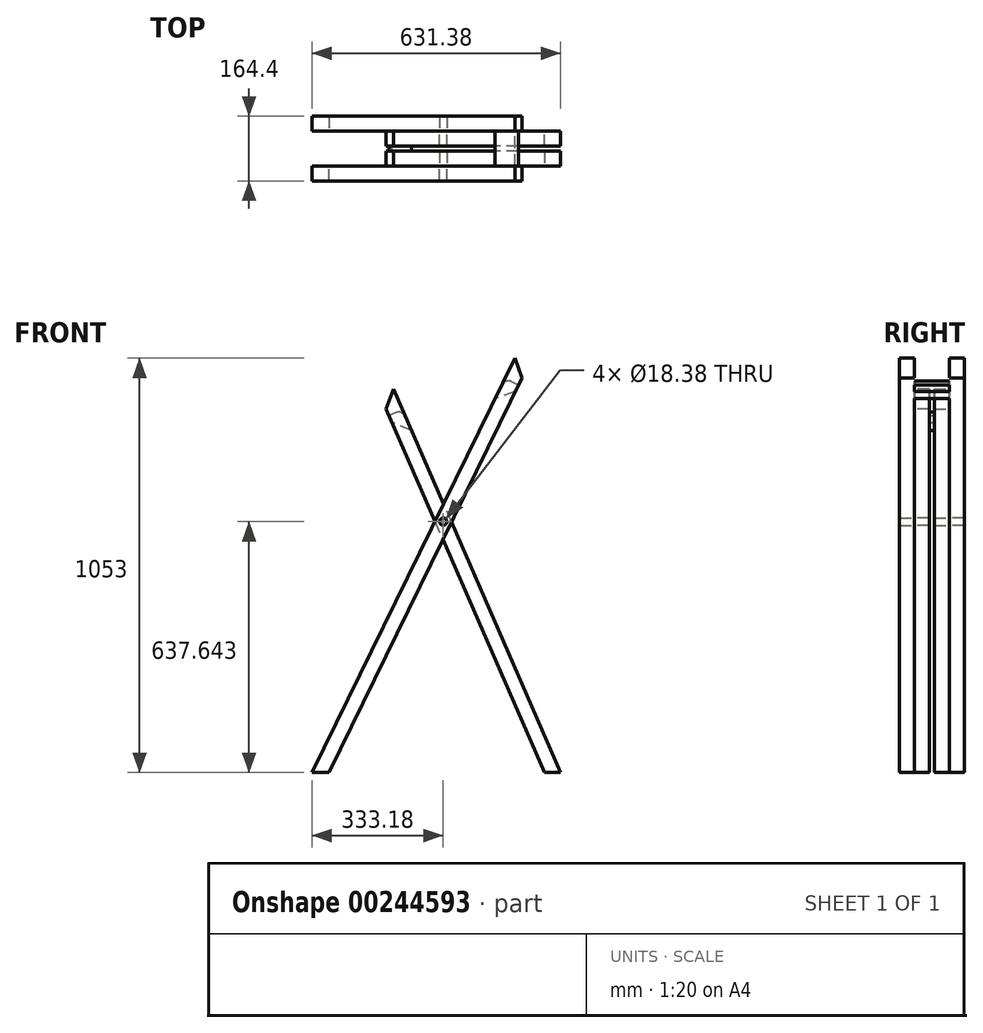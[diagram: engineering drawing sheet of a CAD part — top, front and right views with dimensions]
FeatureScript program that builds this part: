
annotation { "Feature Type Name" : "Feature", "Feature Type Description" : "" }
export const myFeature = defineFeature(function(context is Context, id is Id, definition is map)
    precondition{}
    {
        {
            assignVariable(context, id + "F0", {"name" : "seatWidth", "anyValue" : 12});
        }
        {
            var Q0;
            Q0=qCreatedBy(makeId("Front.planeOp"),FACE);
            var sketch = newSketch(context, id + "F1", { "sketchPlane" : qUnion([Q0])});
            skLineSegment(sketch, "E0", {"start": v(-458.88, 959.2) * mm, "end": v(-443.68, 924.27) * mm, "construction": true});
            skLineSegment(sketch, "E1", {"start": v(-41.55, 0) * mm, "end": v(0, 0) * mm});
            skLineSegment(sketch, "E2", {"start": v(0, 0) * mm, "end": v(-423.94, 974.4) * mm});
            skLineSegment(sketch, "E3", {"start": v(-423.94, 974.4) * mm, "end": v(-458.88, 959.2) * mm, "construction": true});
            skLineSegment(sketch, "E4", {"start": v(-631.38, 0) * mm, "end": v(-588.97, 0) * mm});
            skLineSegment(sketch, "E5", {"start": v(-588.97, 0) * mm, "end": v(-98.71, 1002.03) * mm});
            skLineSegment(sketch, "E6", {"start": v(-81.97, 1036.25) * mm, "end": v(-116.2, 1053) * mm, "construction": true});
            skLineSegment(sketch, "E7", {"start": v(-116.2, 1053) * mm, "end": v(-631.38, 0) * mm});
            skLineSegment(sketch, "E8", {"start": v(-441.41, 966.8) * mm, "end": v(-20.77, 0) * mm, "construction": true});
            skLineSegment(sketch, "E9", {"start": v(-610.17, 0) * mm, "end": v(-99.08, 1044.62) * mm, "construction": true});
            skCircle(sketch, "E10", {"center": v(-298.2, 637.64) * mm, "radius": 9.19 * mm});
            skLineSegment(sketch, "E11", {"start": v(-41.55, 0) * mm, "end": v(-588.97, 0) * mm, "construction": true});
            skLineSegment(sketch, "E12", {"start": v(-418.61, 914.4) * mm, "end": v(-124.2, 993.29) * mm, "construction": true});
            skLineSegment(sketch, "E13", {"start": v(-423.94, 974.4) * mm, "end": v(-443.68, 924.27) * mm});
            skLineSegment(sketch, "E14", {"start": v(-443.68, 924.27) * mm, "end": v(-41.55, 0) * mm});
            skLineSegment(sketch, "E15", {"start": v(-116.2, 1053) * mm, "end": v(-98.71, 1002.03) * mm});
            skLineSegment(sketch, "E16", {"start": v(-98.71, 1002.03) * mm, "end": v(-81.97, 1036.25) * mm, "construction": true});
            skLineSegment(sketch, "E17", {"start": v(-418.61, 914.4) * mm, "end": v(-436.08, 906.8) * mm});
            skLineSegment(sketch, "E18", {"start": v(-436.08, 906.8) * mm, "end": v(-428.48, 889.33) * mm});
            skLineSegment(sketch, "E19", {"start": v(-428.48, 889.33) * mm, "end": v(-378.34, 869.6) * mm});
            skLineSegment(sketch, "E20", {"start": v(-418.61, 914.4) * mm, "end": v(-401.14, 922) * mm});
            skLineSegment(sketch, "E21", {"start": v(-401.14, 922) * mm, "end": v(-378.34, 869.6) * mm});
            skLineSegment(sketch, "E22", {"start": v(-107.09, 984.92) * mm, "end": v(-141.3, 1001.66) * mm});
            skLineSegment(sketch, "E23", {"start": v(-141.3, 1001.66) * mm, "end": v(-166.43, 950.32) * mm});
            skLineSegment(sketch, "E24", {"start": v(-166.43, 950.32) * mm, "end": v(-115.46, 967.8) * mm});
            skLineSegment(sketch, "E25", {"start": v(-115.46, 967.8) * mm, "end": v(-107.09, 984.92) * mm});
            skSolve(sketch);
        }
        {
            var Q0;
            {var subQ0=sQuery(id+"F1.wireOp",EDGE,"E13");Q0=makeQuery(id+"F1.imprint","IMPRINT",FACE,{"disambiguationData":[TD([[makeQuery(id+"F1.imprint","IMPRINT",EDGE,{"derivedFrom":subQ0}),1.0]])]});}
            var Q1;
            {var subQ0=sQuery(id+"F1.wireOp",EDGE,"E7");var subQ1=sQuery(id+"F1.wireOp",EDGE,"E2");var subQ2=makeQuery(id+"F1.imprint","INTERSECT",VERTEX,{"derivedFrom":[subQ1,subQ0]});Q1=makeQuery(id+"F1.imprint","IMPRINT",FACE,{"disambiguationData":[TD([[makeQuery(id+"F1.imprint","IMPRINT",EDGE,{"disambiguationData":[TD([[subQ2,-1.0]])],"derivedFrom":subQ1}),1.0]])]});}
            var Q2;
            {var subQ0=sQuery(id+"F1.wireOp",EDGE,"G5fDf9HS-GnTO-aWqJ-AB5R-3zAjnKYNcMg0");var subQ1=makeQuery(id+"F1.imprint","INTERSECT",VERTEX,{"derivedFrom":[sQuery(id+"F1.wireOp",EDGE,"E2"),subQ0]});Q2=makeQuery(id+"F1.imprint","IMPRINT",FACE,{"disambiguationData":[TD([[makeQuery(id+"F1.imprint","IMPRINT",EDGE,{"disambiguationData":[TD([[subQ1,-1.0]])],"derivedFrom":subQ0}),1.0]])]});}
            var Q3;
            {var subQ0=sQuery(id+"F1.wireOp",EDGE,"E1");Q3=makeQuery(id+"F1.imprint","IMPRINT",FACE,{"disambiguationData":[TD([[makeQuery(id+"F1.imprint","IMPRINT",EDGE,{"derivedFrom":subQ0}),1.0]])]});}
            var Q4;
            Q4=makeQuery(id+"F1.imprint","IMPRINT",FACE,{"disambiguationData":[TD([[makeQuery(id+"F1.imprint","IMPRINT",EDGE,{"derivedFrom":sQuery(id+"F1.wireOp",EDGE,"E10")}),-1.0]])]});
            var Q5;
            Q5=makeQuery(id+"F1.imprint","IMPRINT",FACE,{"disambiguationData":[TD([[makeQuery(id+"F1.imprint","IMPRINT",EDGE,{"derivedFrom":sQuery(id+"F1.wireOp",EDGE,"E17")}),1.0]])]});
            extrude(context, id + "F2", {"entities" : qUnion([Q0, Q1, Q2, Q3, Q4, Q5]), "depth" : 38.1 * mm});
        }
        {
            var Q0;
            {var subQ0=sQuery(id+"F1.wireOp",EDGE,"E6");Q0=makeQuery(id+"F1.imprint","IMPRINT",FACE,{"disambiguationData":[TD([[makeQuery(id+"F1.imprint","IMPRINT",EDGE,{"derivedFrom":subQ0}),1.0]])]});}
            var Q1;
            {var subQ0=sQuery(id+"F1.wireOp",EDGE,"dulVGA2T-eOXA-Yl6J-INj3-XliQijIYnVBT");var subQ1=makeQuery(id+"F1.imprint","INTERSECT",VERTEX,{"derivedFrom":[sQuery(id+"F1.wireOp",EDGE,"E5"),subQ0]});Q1=makeQuery(id+"F1.imprint","IMPRINT",FACE,{"disambiguationData":[TD([[makeQuery(id+"F1.imprint","IMPRINT",EDGE,{"disambiguationData":[TD([[subQ1,1.0]])],"derivedFrom":subQ0}),1.0]])]});}
            var Q2;
            {var subQ0=sQuery(id+"F1.wireOp",EDGE,"E5");var subQ1=sQuery(id+"F1.wireOp",EDGE,"E2");var subQ2=makeQuery(id+"F1.imprint","INTERSECT",VERTEX,{"derivedFrom":[subQ1,subQ0]});Q2=makeQuery(id+"F1.imprint","IMPRINT",FACE,{"disambiguationData":[TD([[makeQuery(id+"F1.imprint","IMPRINT",EDGE,{"disambiguationData":[TD([[subQ2,-1.0]])],"derivedFrom":subQ1}),-1.0]])]});}
            var Q3;
            {var subQ5=sQuery(id+"F1.wireOp",EDGE,"E4");Q3=makeQuery(id+"F1.imprint","IMPRINT",FACE,{"disambiguationData":[TD([[makeQuery(id+"F1.imprint","IMPRINT",EDGE,{"derivedFrom":subQ5}),1.0]])]});}
            var Q4;
            Q4=makeQuery(id+"F1.imprint","IMPRINT",FACE,{"disambiguationData":[TD([[makeQuery(id+"F1.imprint","IMPRINT",EDGE,{"derivedFrom":sQuery(id+"F1.wireOp",EDGE,"E10")}),-1.0]])]});
            var Q5;
            {var subQ0=sQuery(id+"F1.wireOp",EDGE,"E15");Q5=makeQuery(id+"F1.imprint","IMPRINT",FACE,{"disambiguationData":[TD([[makeQuery(id+"F1.imprint","IMPRINT",EDGE,{"derivedFrom":subQ0}),-1.0]])]});}
            var Q6;
            Q6=makeQuery(id+"F1.imprint","IMPRINT",FACE,{"disambiguationData":[TD([[makeQuery(id+"F1.imprint","IMPRINT",EDGE,{"derivedFrom":sQuery(id+"F1.wireOp",EDGE,"E22")}),1.0]])]});
            extrude(context, id + "F3", {"entities" : qUnion([Q0, Q1, Q2, Q3, Q4, Q5, Q6]), "oppositeDirection" : true, "depth" : 38.1 * mm});
        }
        {
            var Q0;
            Q0=makeQuery(id+"F2.opExtrude","CAP_FACE",FACE,{"disambiguationData":[OSD([sQuery(id+"F1.wireOp",EDGE,"E1"),sQuery(id+"F1.wireOp",EDGE,"E2"),sQuery(id+"F1.wireOp",EDGE,"E10"),sQuery(id+"F1.wireOp",EDGE,"E13"),sQuery(id+"F1.wireOp",EDGE,"E14"),sQuery(id+"F1.wireOp",EDGE,"E18"),sQuery(id+"F1.wireOp",EDGE,"E21")])],"isStart":false});
            var sketch = newSketch(context, id + "F4", { "sketchPlane" : qUnion([Q0])});
            skLineSegment(sketch, "E26.0", {"start": v(-418.61, 914.4) * mm, "end": v(-436.08, 906.8) * mm});
            skLineSegment(sketch, "E26.1", {"start": v(-418.61, 914.4) * mm, "end": v(-401.14, 922) * mm});
            skLineSegment(sketch, "E26.2", {"start": v(-401.14, 922) * mm, "end": v(-378.34, 869.6) * mm});
            skLineSegment(sketch, "E26.3", {"start": v(-428.48, 889.33) * mm, "end": v(-378.34, 869.6) * mm});
            skLineSegment(sketch, "E26.4", {"start": v(-436.08, 906.8) * mm, "end": v(-428.48, 889.33) * mm});
            skSolve(sketch);
        }
        {
            var Q0;
            Q0=makeQuery(id+"F2.opExtrude","CAP_FACE",FACE,{"disambiguationData":[OSD([sQuery(id+"F1.wireOp",EDGE,"E0"),sQuery(id+"F1.wireOp",EDGE,"E1"),sQuery(id+"F1.wireOp",EDGE,"E2"),sQuery(id+"F1.wireOp",EDGE,"E3"),sQuery(id+"F1.wireOp",EDGE,"E10")])],"isStart":false});
            cPlane(context, id + "F5", {"entities" : qUnion([Q0]), "cplaneType" : CPlaneType.OFFSET, "offset" : (getVariable(context, 'seatWidth') / 2) * mm, "width" : 152.4 * mm, "height" : 152.4 * mm});
        }
        {
            var Q0;
            Q0=makeQuery(id+"F3.opExtrude","SWEPT_BODY",BODY,{"disambiguationData":[OSD([sQuery(id+"F1.wireOp",EDGE,"E4"),sQuery(id+"F1.wireOp",EDGE,"E5"),sQuery(id+"F1.wireOp",EDGE,"E6"),sQuery(id+"F1.wireOp",EDGE,"E7"),sQuery(id+"F1.wireOp",EDGE,"E10")])]});
            var Q1;
            Q1=makeQuery(id+"F2.opExtrude","SWEPT_BODY",BODY,{"disambiguationData":[OSD([sQuery(id+"F1.wireOp",EDGE,"E0"),sQuery(id+"F1.wireOp",EDGE,"E1"),sQuery(id+"F1.wireOp",EDGE,"E2"),sQuery(id+"F1.wireOp",EDGE,"E3"),sQuery(id+"F1.wireOp",EDGE,"E10")])]});
            var Q2;
            Q2=qCreatedBy(id+"F5.planeOp",FACE);
            mirror(context, id + "F6", {"entities" : qUnion([Q0, Q1]), "mirrorPlane" : qUnion([Q2])});
        }
        {
            var Q0;
            Q0=makeQuery(id+"F4.imprint","IMPRINT",FACE,{"disambiguationData":[TD([[makeQuery(id+"F4.imprint","IMPRINT",EDGE,{"derivedFrom":sQuery(id+"F4.wireOp",EDGE,"E26.0")}),1.0]])]});
            var Q1;
            Q1=makeQuery(id+"F6.opPattern","COPY",BODY,{"derivedFrom":makeQuery(id+"F2.opExtrude","SWEPT_BODY",BODY,{"disambiguationData":[OSD([sQuery(id+"F1.wireOp",EDGE,"E1"),sQuery(id+"F1.wireOp",EDGE,"E2"),sQuery(id+"F1.wireOp",EDGE,"E10"),sQuery(id+"F1.wireOp",EDGE,"E13"),sQuery(id+"F1.wireOp",EDGE,"E14"),sQuery(id+"F1.wireOp",EDGE,"E18"),sQuery(id+"F1.wireOp",EDGE,"E21")])]}),"instanceName":"1"});
            extrude(context, id + "F7", {"entities" : qUnion([Q0]), "endBound" : BoundingType.UP_TO_BODY, "endBoundEntityBody" : qUnion([Q1]), "depth" : 25.4 * mm});
        }
        {
            var Q0;
            Q0=makeQuery(id+"F1.imprint","IMPRINT",FACE,{"disambiguationData":[TD([[makeQuery(id+"F1.imprint","IMPRINT",EDGE,{"derivedFrom":sQuery(id+"F1.wireOp",EDGE,"E22")}),1.0]])]});
            var Q1;
            Q1=makeQuery(id+"F6.opPattern","COPY",BODY,{"derivedFrom":makeQuery(id+"F3.opExtrude","SWEPT_BODY",BODY,{"disambiguationData":[OSD([sQuery(id+"F1.wireOp",EDGE,"E4"),sQuery(id+"F1.wireOp",EDGE,"E5"),sQuery(id+"F1.wireOp",EDGE,"E7"),sQuery(id+"F1.wireOp",EDGE,"E10"),sQuery(id+"F1.wireOp",EDGE,"E15"),sQuery(id+"F1.wireOp",EDGE,"E23"),sQuery(id+"F1.wireOp",EDGE,"E25")])]}),"instanceName":"1"});
            extrude(context, id + "F8", {"entities" : qUnion([Q0]), "endBound" : BoundingType.UP_TO_BODY, "endBoundEntityBody" : qUnion([Q1]), "depth" : 25.4 * mm});
        }
        {
            var Q0;
            Q0=makeQuery(id+"F7.opExtrude","SWEPT_EDGE",EDGE,{"disambiguationData":[OSD([sQuery(id+"F1.wireOp",EDGE,"E2"),sQuery(id+"F1.wireOp",EDGE,"E21"),sQuery(id+"F4.wireOp",EDGE,"E26.1"),sQuery(id+"F4.wireOp",EDGE,"E26.2")])]});
            var Q1;
            Q1=makeQuery(id+"F8.opExtrude","SWEPT_EDGE",EDGE,{"disambiguationData":[OSD([sQuery(id+"F1.wireOp",EDGE,"E7"),sQuery(id+"F1.wireOp",EDGE,"E22"),sQuery(id+"F1.wireOp",EDGE,"E23")])]});
            fillet(context, id + "F9", {"entities" : qUnion([Q0, Q1]), "radius" : 19.05 * mm, "tangentPropagation" : true, "allowEdgeOverflow" : false});
        }
    });
